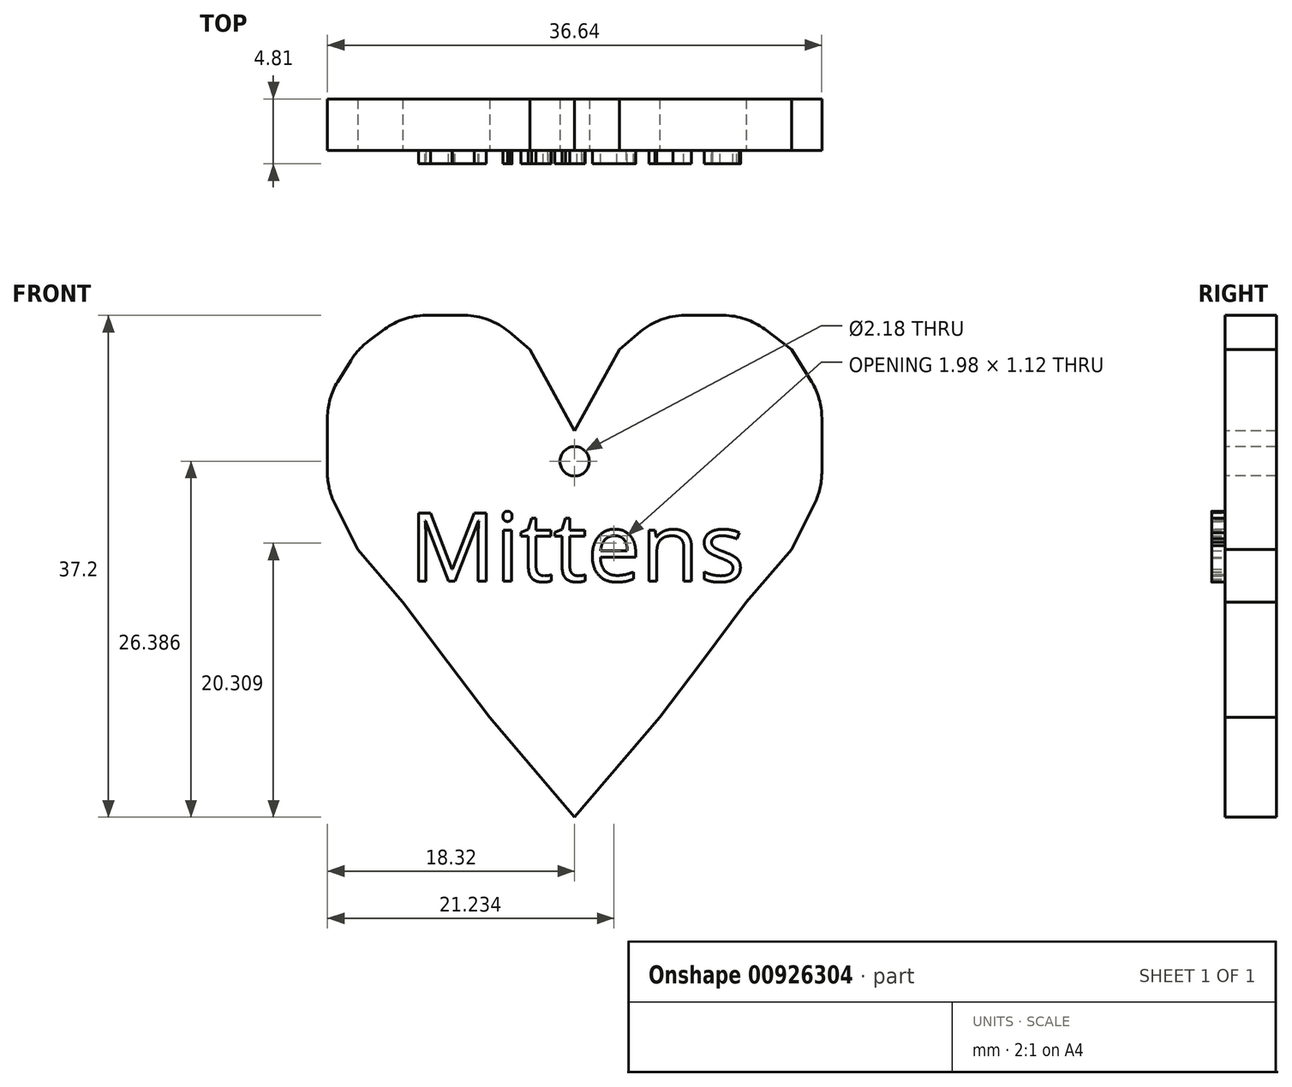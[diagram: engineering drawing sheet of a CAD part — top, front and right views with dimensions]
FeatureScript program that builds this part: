
annotation { "Feature Type Name" : "Feature", "Feature Type Description" : "" }
export const myFeature = defineFeature(function(context is Context, id is Id, definition is map)
    precondition{}
    {
        {
            var Q0;
            Q0=qCreatedBy(makeId("Front.planeOp"),FACE);
            var sketch = newSketch(context, id + "F0", { "sketchPlane" : qUnion([Q0])});
            skLineSegment(sketch, "E0", {"start": v(0, 48.82) * mm, "end": v(0, -29.8) * mm, "construction": true});
            skLineSegment(sketch, "E1", {"start": v(0, 21.24) * mm, "end": v(3.32, 27.28) * mm});
            skLineSegment(sketch, "E2", {"start": v(3.32, 27.28) * mm, "end": v(6.3, 29.8) * mm});
            skLineSegment(sketch, "E3", {"start": v(6.3, 29.8) * mm, "end": v(9.37, 29.8) * mm});
            skLineSegment(sketch, "E4", {"start": v(9.37, 29.8) * mm, "end": v(12.73, 29.8) * mm});
            skLineSegment(sketch, "E5", {"start": v(12.73, 29.8) * mm, "end": v(16.09, 27.28) * mm});
            skLineSegment(sketch, "E6", {"start": v(16.09, 27.28) * mm, "end": v(18.32, 23.64) * mm});
            skLineSegment(sketch, "E7", {"start": v(18.32, 23.64) * mm, "end": v(18.32, 19.72) * mm});
            skLineSegment(sketch, "E8", {"start": v(18.32, 19.72) * mm, "end": v(18.32, 16.93) * mm});
            skLineSegment(sketch, "E9", {"start": v(18.32, 16.93) * mm, "end": v(16.09, 12.45) * mm});
            skLineSegment(sketch, "E10", {"start": v(16.09, 12.45) * mm, "end": v(12.73, 8.53) * mm});
            skLineSegment(sketch, "E11", {"start": v(12.73, 8.53) * mm, "end": v(9.37, 4.06) * mm});
            skLineSegment(sketch, "E12", {"start": v(9.37, 4.06) * mm, "end": v(6.3, 0) * mm});
            skLineSegment(sketch, "E13", {"start": v(6.3, 0) * mm, "end": v(0, -7.41) * mm});
            skLineSegment(sketch, "E14.MirrorCS", {"start": v(-9.37, 4.06) * mm, "end": v(-6.3, 0) * mm});
            skLineSegment(sketch, "E15.MirrorCS", {"start": v(-16.09, 27.28) * mm, "end": v(-18.32, 23.64) * mm});
            skLineSegment(sketch, "E16.MirrorCS", {"start": v(-12.73, 29.8) * mm, "end": v(-16.09, 27.28) * mm});
            skLineSegment(sketch, "E17.MirrorCS", {"start": v(-18.32, 16.93) * mm, "end": v(-16.09, 12.45) * mm});
            skLineSegment(sketch, "E18.MirrorCS", {"start": v(-16.09, 12.45) * mm, "end": v(-12.73, 8.53) * mm});
            skLineSegment(sketch, "E19.MirrorCS", {"start": v(-18.32, 19.72) * mm, "end": v(-18.32, 16.93) * mm});
            skLineSegment(sketch, "E20.MirrorCS", {"start": v(-3.32, 27.28) * mm, "end": v(-6.3, 29.8) * mm});
            skLineSegment(sketch, "E21.MirrorCS", {"start": v(0, 21.24) * mm, "end": v(-3.32, 27.28) * mm});
            skLineSegment(sketch, "E22.MirrorCS", {"start": v(-9.37, 29.8) * mm, "end": v(-12.73, 29.8) * mm});
            skLineSegment(sketch, "E23.MirrorCS", {"start": v(-12.73, 8.53) * mm, "end": v(-9.37, 4.06) * mm});
            skLineSegment(sketch, "E24.MirrorCS", {"start": v(-6.3, 29.8) * mm, "end": v(-9.37, 29.8) * mm});
            skLineSegment(sketch, "E25.MirrorCS", {"start": v(-18.32, 23.64) * mm, "end": v(-18.32, 19.72) * mm});
            skLineSegment(sketch, "E26.MirrorCS", {"start": v(-6.3, 0) * mm, "end": v(0, -7.41) * mm});
            skCircle(sketch, "E27", {"center": v(0, 18.98) * mm, "radius": 1.09 * mm});
            skSolve(sketch);
        }
        {
            var Q0;
            Q0=makeQuery(id+"F0.imprint","IMPRINT",FACE,{"disambiguationData":[TD([[makeQuery(id+"F0.imprint","IMPRINT",EDGE,{"derivedFrom":sQuery(id+"F0.wireOp",EDGE,"E1")}),-1.0]])]});
            extrude(context, id + "F1", {"entities" : qUnion([Q0]), "oppositeDirection" : true, "depth" : 3.8 * mm, "offsetDistance" : 25.4 * mm});
        }
        {
            var Q0;
            Q0=makeQuery(id+"F0.imprint","IMPRINT",FACE,{"disambiguationData":[TD([[makeQuery(id+"F0.imprint","IMPRINT",EDGE,{"derivedFrom":sQuery(id+"F0.wireOp",EDGE,"E1")}),-1.0]])]});
            var sketch = newSketch(context, id + "F2", { "sketchPlane" : qUnion([Q0])});
            skText(sketch, "E28", { "text": "Mittens\n", "fontName": "OpenSans-Regular.ttf"});
            const initialGuessF2  = {"E28": [-0.01227, 0.01008, 1, 0, 0.0051]};
            skSetInitialGuess(sketch, initialGuessF2);
            skSolve(sketch);
        }
        {
            var Q0;
            Q0 = qSketchRegion(id + "F2", true);
            extrude(context, id + "F3", {"entities" : qUnion([Q0]), "depth" : 1 * mm, "offsetDistance" : 25.4 * mm});
        }
        {
            var Q0;
            Q0=makeQuery(id+"F1.opExtrude","CAP_FACE",FACE,{"disambiguationData":[OSD([sQuery(id+"F0.wireOp",EDGE,"E1"),sQuery(id+"F0.wireOp",EDGE,"E2"),sQuery(id+"F0.wireOp",EDGE,"E3"),sQuery(id+"F0.wireOp",EDGE,"E4"),sQuery(id+"F0.wireOp",EDGE,"E5"),sQuery(id+"F0.wireOp",EDGE,"E6"),sQuery(id+"F0.wireOp",EDGE,"E7"),sQuery(id+"F0.wireOp",EDGE,"E8"),sQuery(id+"F0.wireOp",EDGE,"E9"),sQuery(id+"F0.wireOp",EDGE,"E10"),sQuery(id+"F0.wireOp",EDGE,"E11"),sQuery(id+"F0.wireOp",EDGE,"E12"),sQuery(id+"F0.wireOp",EDGE,"E13"),sQuery(id+"F0.wireOp",EDGE,"E14.MirrorCS"),sQuery(id+"F0.wireOp",EDGE,"E15.MirrorCS"),sQuery(id+"F0.wireOp",EDGE,"E16.MirrorCS"),sQuery(id+"F0.wireOp",EDGE,"E17.MirrorCS"),sQuery(id+"F0.wireOp",EDGE,"E18.MirrorCS"),sQuery(id+"F0.wireOp",EDGE,"E19.MirrorCS"),sQuery(id+"F0.wireOp",EDGE,"E20.MirrorCS"),sQuery(id+"F0.wireOp",EDGE,"E21.MirrorCS"),sQuery(id+"F0.wireOp",EDGE,"E22.MirrorCS"),sQuery(id+"F0.wireOp",EDGE,"E23.MirrorCS"),sQuery(id+"F0.wireOp",EDGE,"E24.MirrorCS"),sQuery(id+"F0.wireOp",EDGE,"E25.MirrorCS"),sQuery(id+"F0.wireOp",EDGE,"E26.MirrorCS"),sQuery(id+"F0.wireOp",EDGE,"E27")])],"isStart":false});
            var sketch = newSketch(context, id + "F4", { "sketchPlane" : qUnion([Q0])});
            skText(sketch, "E29", { "text": "40 Marsten Ln\nunit 114\nEnfield,NH 03748", "fontName": "OpenSans-Regular.ttf"});
            const initialGuessF4  = {"E29": [-0.00995, 0.01296, 1, 0, 0.00178]};
            skSetInitialGuess(sketch, initialGuessF4);
            skSolve(sketch);
        }
        {
            var Q0;
            Q0 = qSketchRegion(id + "F4", true);
            extrude(context, id + "F5", {"entities" : qUnion([Q0]), "operationType" : NewBodyOperationType.REMOVE, "depth" : 0.3 * mm, "offsetDistance" : 25.4 * mm});
        }
        {
            var Q0;
            Q0=makeQuery(id+"F1.opExtrude","SWEPT_EDGE",EDGE,{"disambiguationData":[OSD([sQuery(id+"F0.wireOp",EDGE,"E4"),sQuery(id+"F0.wireOp",EDGE,"E5")])]});
            var Q1;
            Q1=makeQuery(id+"F1.opExtrude","SWEPT_EDGE",EDGE,{"disambiguationData":[OSD([sQuery(id+"F0.wireOp",EDGE,"E2"),sQuery(id+"F0.wireOp",EDGE,"E3")])]});
            fillet(context, id + "F6", {"entities" : qUnion([Q0, Q1]), "radius" : 5.08 * mm, "tangentPropagation" : true, "allowEdgeOverflow" : false});
        }
        {
            var Q0;
            Q0=makeQuery(id+"F1.opExtrude","SWEPT_EDGE",EDGE,{"disambiguationData":[OSD([sQuery(id+"F0.wireOp",EDGE,"E6"),sQuery(id+"F0.wireOp",EDGE,"E7")])]});
            fillet(context, id + "F7", {"entities" : qUnion([Q0]), "radius" : 5.08 * mm, "tangentPropagation" : true, "allowEdgeOverflow" : false});
        }
        {
            var Q0;
            Q0=makeQuery(id+"F1.opExtrude","SWEPT_EDGE",EDGE,{"disambiguationData":[OSD([sQuery(id+"F0.wireOp",EDGE,"E8"),sQuery(id+"F0.wireOp",EDGE,"E9")])]});
            fillet(context, id + "F8", {"entities" : qUnion([Q0]), "radius" : 5.08 * mm, "tangentPropagation" : true, "allowEdgeOverflow" : false});
        }
        {
            var Q0;
            Q0=makeQuery(id+"F1.opExtrude","SWEPT_EDGE",EDGE,{"disambiguationData":[OSD([sQuery(id+"F0.wireOp",EDGE,"E20.MirrorCS"),sQuery(id+"F0.wireOp",EDGE,"E24.MirrorCS")])]});
            fillet(context, id + "F9", {"entities" : qUnion([Q0]), "radius" : 5.08 * mm, "tangentPropagation" : true, "allowEdgeOverflow" : false});
        }
        {
            var Q0;
            Q0=makeQuery(id+"F1.opExtrude","SWEPT_EDGE",EDGE,{"disambiguationData":[OSD([sQuery(id+"F0.wireOp",EDGE,"E16.MirrorCS"),sQuery(id+"F0.wireOp",EDGE,"E22.MirrorCS")])]});
            fillet(context, id + "F10", {"entities" : qUnion([Q0]), "radius" : 5.08 * mm, "tangentPropagation" : true, "allowEdgeOverflow" : false});
        }
        {
            var Q0;
            Q0=makeQuery(id+"F1.opExtrude","SWEPT_EDGE",EDGE,{"disambiguationData":[OSD([sQuery(id+"F0.wireOp",EDGE,"E15.MirrorCS"),sQuery(id+"F0.wireOp",EDGE,"E16.MirrorCS")])]});
            fillet(context, id + "F11", {"entities" : qUnion([Q0]), "radius" : 5.08 * mm, "tangentPropagation" : true, "allowEdgeOverflow" : false});
        }
        {
            var Q0;
            Q0=makeQuery(id+"F1.opExtrude","SWEPT_EDGE",EDGE,{"disambiguationData":[OSD([sQuery(id+"F0.wireOp",EDGE,"E15.MirrorCS"),sQuery(id+"F0.wireOp",EDGE,"E25.MirrorCS")])]});
            fillet(context, id + "F12", {"entities" : qUnion([Q0]), "radius" : 5.08 * mm, "tangentPropagation" : true, "allowEdgeOverflow" : false});
        }
        {
            var Q0;
            Q0=makeQuery(id+"F1.opExtrude","SWEPT_EDGE",EDGE,{"disambiguationData":[OSD([sQuery(id+"F0.wireOp",EDGE,"E17.MirrorCS"),sQuery(id+"F0.wireOp",EDGE,"E19.MirrorCS")])]});
            fillet(context, id + "F13", {"entities" : qUnion([Q0]), "radius" : 5.08 * mm, "tangentPropagation" : true, "allowEdgeOverflow" : false});
        }
    });
